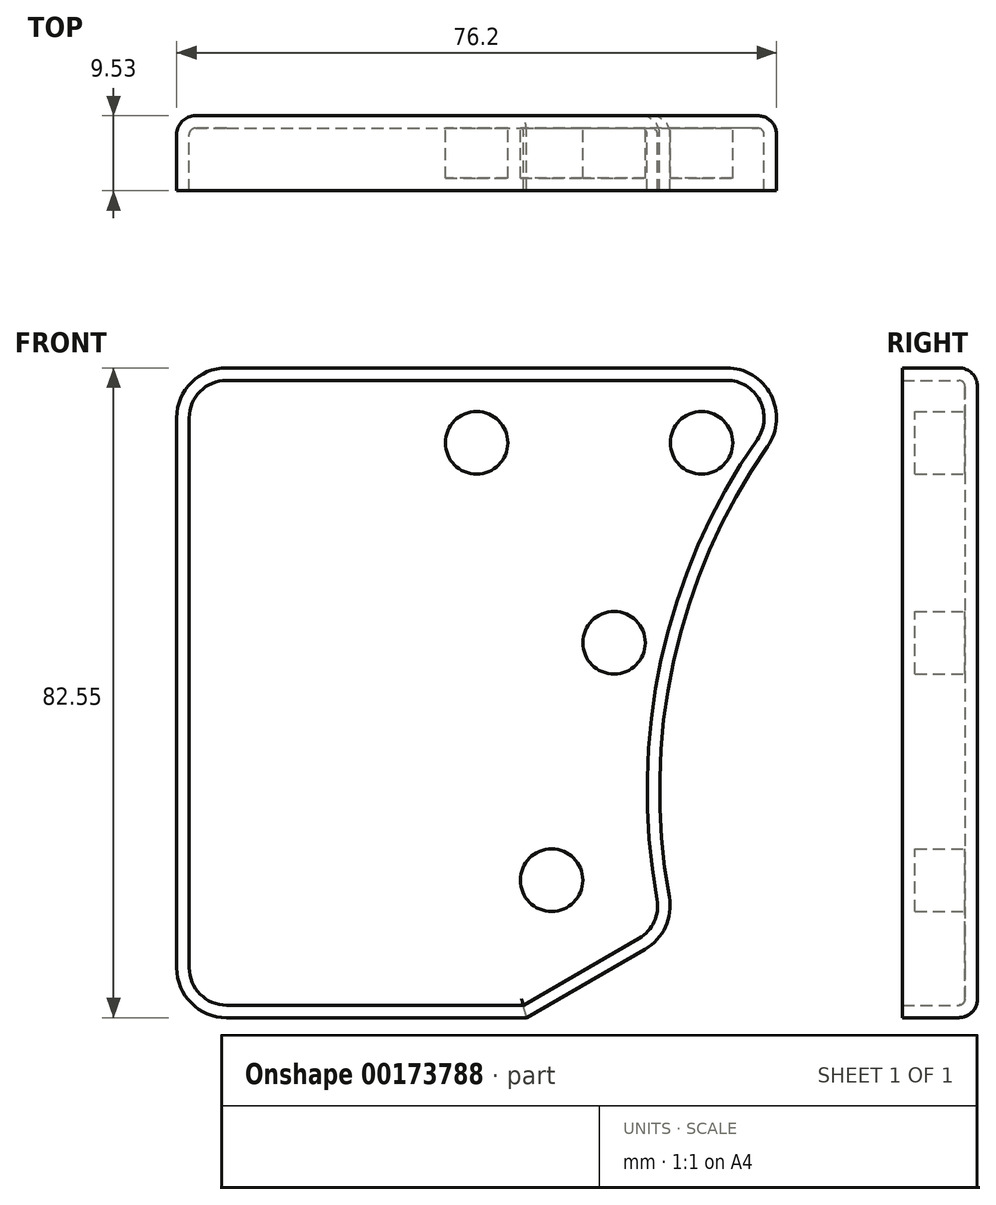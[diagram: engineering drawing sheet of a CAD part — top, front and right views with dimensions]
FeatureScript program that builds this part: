
annotation { "Feature Type Name" : "Feature", "Feature Type Description" : "" }
export const myFeature = defineFeature(function(context is Context, id is Id, definition is map)
    precondition{}
    {
        {
            var Q0;
            Q0=qCreatedBy(makeId("Front.planeOp"),FACE);
            var sketch = newSketch(context, id + "F0", { "sketchPlane" : qUnion([Q0])});
            skLineSegment(sketch, "E0", {"start": v(-19.05, 0) * mm, "end": v(44.45, 0) * mm});
            skLineSegment(sketch, "E1", {"start": v(-25.4, -6.35) * mm, "end": v(-25.4, -76.2) * mm});
            skLineSegment(sketch, "E2", {"start": v(-19.05, -82.55) * mm, "end": v(19.05, -82.55) * mm});
            skArc(sketch, "E3", {"start": v(49.66, -9.98) * mm, "mid": v(50.08, -3.41) * mm, "end": v(44.45, 0) * mm});
            skLineSegment(sketch, "E4", {"start": v(19.05, -82.55) * mm, "end": v(34.1, -73.86) * mm});
            skLineSegment(sketch, "E5", {"start": v(38.1, -71.55) * mm, "end": v(38.1, -82.55) * mm, "construction": true});
            skLineSegment(sketch, "E6", {"start": v(38.1, -82.55) * mm, "end": v(19.05, -82.55) * mm, "construction": true});
            skArc(sketch, "E7", {"start": v(49.66, -9.98) * mm, "mid": v(37.7, -37.35) * mm, "end": v(37.18, -67.22) * mm});
            skPoint(sketch, "E8.visualSharp", {"position": v(38.1, -71.55) * mm});
            skArc(sketch, "E8.filletArc", {"start": v(34.1, -73.86) * mm, "mid": v(36.7, -71.02) * mm, "end": v(37.18, -67.22) * mm});
            skPoint(sketch, "E9", {"position": v(50.8, -6.35) * mm});
            skPoint(sketch, "E10.visualSharp", {"position": v(-25.4, 0) * mm});
            skArc(sketch, "E10.filletArc", {"start": v(-19.05, 0) * mm, "mid": v(-23.54, -1.86) * mm, "end": v(-25.4, -6.35) * mm});
            skPoint(sketch, "E11.visualSharp", {"position": v(-25.4, -82.55) * mm});
            skArc(sketch, "E11.filletArc", {"start": v(-25.4, -76.2) * mm, "mid": v(-23.54, -80.7) * mm, "end": v(-19.05, -82.55) * mm});
            skSolve(sketch);
        }
        {
            var Q0;
            Q0=makeQuery(id+"F0.imprint","IMPRINT",FACE,{"disambiguationData":[TD([[makeQuery(id+"F0.imprint","IMPRINT",EDGE,{"derivedFrom":sQuery(id+"F0.wireOp",EDGE,"E0")}),-1.0]])]});
            extrude(context, id + "F1", {"entities" : qUnion([Q0]), "depth" : 9.52 * mm});
        }
        {
            var Q0;
            Q0=makeQuery(id+"F1.opExtrude","CAP_FACE",FACE,{"disambiguationData":[OSD([sQuery(id+"F0.wireOp",EDGE,"E0"),sQuery(id+"F0.wireOp",EDGE,"E1"),sQuery(id+"F0.wireOp",EDGE,"E2"),sQuery(id+"F0.wireOp",EDGE,"E3"),sQuery(id+"F0.wireOp",EDGE,"E4"),sQuery(id+"F0.wireOp",EDGE,"E7"),sQuery(id+"F0.wireOp",EDGE,"E8.filletArc"),sQuery(id+"F0.wireOp",EDGE,"E10.filletArc"),sQuery(id+"F0.wireOp",EDGE,"E11.filletArc")])],"isStart":false});
            shell(context, id + "F2", {"entities" : qUnion([Q0]), "thickness" : 1.59 * mm});
        }
        {
            var Q0;
            Q0=makeQuery(id+"F2.opShell","OFFSET_FACE",FACE,{"disambiguationData":[OSD([sQuery(id+"F0.wireOp",EDGE,"E0"),sQuery(id+"F0.wireOp",EDGE,"E1"),sQuery(id+"F0.wireOp",EDGE,"E2"),sQuery(id+"F0.wireOp",EDGE,"E3"),sQuery(id+"F0.wireOp",EDGE,"E4"),sQuery(id+"F0.wireOp",EDGE,"E7"),sQuery(id+"F0.wireOp",EDGE,"E8.filletArc"),sQuery(id+"F0.wireOp",EDGE,"E10.filletArc"),sQuery(id+"F0.wireOp",EDGE,"E11.filletArc")])]});
            var sketch = newSketch(context, id + "F3", { "sketchPlane" : qUnion([Q0])});
            skCircle(sketch, "E12", {"center": v(41.28, -9.52) * mm, "radius": 3.97 * mm});
            skCircle(sketch, "E13", {"center": v(12.7, -9.53) * mm, "radius": 3.97 * mm});
            skCircle(sketch, "E14", {"center": v(30.16, -34.93) * mm, "radius": 3.97 * mm});
            skLineSegment(sketch, "E15", {"start": v(41.28, -9.52) * mm, "end": v(12.7, -9.53) * mm, "construction": true});
            skCircle(sketch, "E16", {"center": v(22.23, -65.09) * mm, "radius": 3.97 * mm});
            skSolve(sketch);
        }
        {
            var Q0;
            Q0=makeQuery(id+"F3.imprint","IMPRINT",FACE,{"disambiguationData":[TD([[makeQuery(id+"F3.imprint","IMPRINT",EDGE,{"derivedFrom":sQuery(id+"F3.wireOp",EDGE,"E12")}),1.0]])]});
            var Q1;
            Q1=makeQuery(id+"F3.imprint","IMPRINT",FACE,{"disambiguationData":[TD([[makeQuery(id+"F3.imprint","IMPRINT",EDGE,{"derivedFrom":sQuery(id+"F3.wireOp",EDGE,"E13")}),1.0]])]});
            var Q2;
            Q2=makeQuery(id+"F3.imprint","IMPRINT",FACE,{"disambiguationData":[TD([[makeQuery(id+"F3.imprint","IMPRINT",EDGE,{"derivedFrom":sQuery(id+"F3.wireOp",EDGE,"E14")}),1.0]])]});
            var Q3;
            Q3=makeQuery(id+"F3.imprint","IMPRINT",FACE,{"disambiguationData":[TD([[makeQuery(id+"F3.imprint","IMPRINT",EDGE,{"derivedFrom":sQuery(id+"F3.wireOp",EDGE,"E16")}),1.0]])]});
            extrude(context, id + "F4", {"entities" : qUnion([Q0, Q1, Q2, Q3]), "operationType" : NewBodyOperationType.ADD, "depth" : 6.35 * mm});
        }
        {
            var Q0;
            {var subQ0=sQuery(id+"F0.wireOp",EDGE,"E1");Q0=makeQuery(id+"F2.opShell","OFFSET_EDGE",EDGE,{"disambiguationData":[OSD([subQ0]),TDD([makeQuery(id+"F1.opExtrude","CAP_EDGE",EDGE,{"disambiguationData":[OSD([subQ0])],"isStart":true})])]});}
            fillet(context, id + "F5", {"entities" : qUnion([Q0]), "radius" : 0.8 * mm, "tangentPropagation" : true, "allowEdgeOverflow" : false});
        }
        {
            var Q0;
            Q0=makeQuery(id+"F1.opExtrude","CAP_EDGE",EDGE,{"disambiguationData":[OSD([sQuery(id+"F0.wireOp",EDGE,"E7")])],"isStart":true});
            fillet(context, id + "F6", {"entities" : qUnion([Q0]), "radius" : 2.38 * mm, "tangentPropagation" : true, "allowEdgeOverflow" : false});
        }
    });
